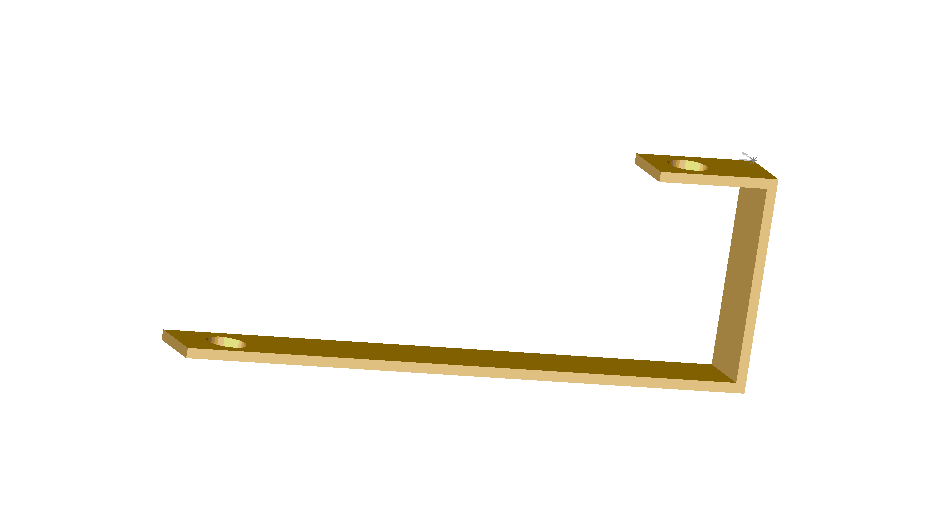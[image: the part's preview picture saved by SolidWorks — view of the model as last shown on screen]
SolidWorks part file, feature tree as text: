
SOLIDWORKS PART (.sldprt)
format: sldprt  version: not decoded by parser v0  size: 131,584 bytes
history: native  units: mm
features: sketch x5, extrude x3, cut_extrude x2 (+8 scaffold rows collapsed)
feature tree (18):
  scaffold x8  (default folders/planes/origin — collapsed)
  sketch  "Sketch19"  dims[D1=129.0mm]
  extrude  "Base-Extrude"  Depth=10mm
  sketch  "Sketch20"  dims[D1=~13.665689mm]
  extrude  "Boss-Extrude1"  Depth=200mm
  sketch  "Sketch21"  dims[D1=~17.414444mm]
  extrude  "Boss-Extrude2"  Depth=560mm
  sketch  "Sketch22"  dims[D1=~23.216031mm]
  cut_extrude  "Cut-Extrude1"  Depth=560mm
  sketch  "Sketch23"  dims[D1=~19.121894mm]
  cut_extrude  "Cut-Extrude2"  Depth=560mm
decode coverage: 10 of 10 modeling features carry decoded parameters
note: ~ marks probable driven/reference dimensions
note: suppression state not decoded; provenance and decode notes live in map.json
